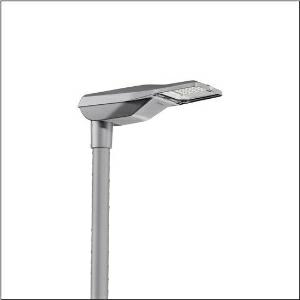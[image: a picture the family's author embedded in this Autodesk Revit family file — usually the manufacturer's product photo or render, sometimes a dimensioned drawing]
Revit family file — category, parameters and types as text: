
# Revit family: streetlight_sl_21_iq_micro___stw1_0a_5xe1e41g08cb_8385
name_source: partatom
category: Lighting Fixtures
units: mm (PartAtom-declared; Revit-internal decimal feet)

## family parameters
Cut with Voids When Loaded = No
Host = Face
Light Source = No
Part Type = Normal
Room Calculation Point = No
Round Connector Dimension = Use Diameter
Shared = No

## types (1)
- --- (1 x LED, 2980 lm, 19.4 W, 4000K)
    Apparent Load = 19 VA
    CIE Flux Codes = 38 75 98 100 100
    Color Rendering = 70
    Color Temperature = 4000K
    Default Elevation = 1800 mm
    Description = Streetlight SL 21 iQ micro, mast luminaire, primary light control with lens, of PMMA, primary optical cover: cover, of toughened safety glass, transparent, light distribution: STW1.0a, light emission: direct distribution, primary light characteristic: asymmetric, installation type: post-top, side-entry, LED, High Power LED, rated luminous flux: 2.980lm, luminous efficacy: 154lm/W, light colour: 740, colour temperature: 4000K, control gear: iQ Street-Remote, control: Street-Remote, Auto-Match, Temp-Guard, Lumen-Switch, Night-Set, Smart-Wire, Light-Fading, Desk-Remote (wireless, voltage-free reading and setting of iQ features in the workshop via application-optimized NFC function/RFID function), optimised constant luminous flux control (CLO 2.0), pre-setting: linear dimming characteristic, mains connection: 220..240V, AC, 50/60Hz, start of lifetime: 19W, end of service life: 20W, reduction: 10W, luminaire housing, of diecast aluminium, powder-coated, SITECO metallic grey (DB 702S), corrosivity category C5 high according to DIN EN ISO 12944, please order mast flange separately, inclination adjustable: 0°, 5°, 10°, 15°, sealing non-destructively replaceable, multi-level sealing system, length: 528mm, width: 235mm, height: 110mm, mast flange for spigot size: 42mm (side-entry): 5XC10008XM4, 60/48mm (side-entry/post-top): 5XC10108XM2, 76/60mm (side-entry/post-top): 5XC10108XM1, protection rating (complete): IP66, insulation class (complete): insulation class II (safety insulation), certification: CE, ENEC, ENEC+, VDE, impact resistance: IK10, permissible operating ambient temperature for outdoor applications: -40..+50°C, standard-compliant lighting for roads and squares, packaging unit: 1 piece

Light Distribution: STW1.0a
    Height = 110 mm
    Lamp = 1 x LED
    Lamp Light Flux = 2980 lm
    Lamp Power = 19.4 W
    Lamp count = 1
    Length = 528 mm
    Luminous efficacy = 154 lm/W
    Manufacturer = Siteco
    ModVariant = No
    Model = 5XE1E41G08CB
    Number of Poles = 1
    OnlyDefault = Yes
    Power Factor = 1
    Product Name = Streetlight SL 21 iQ micro | STW1.0a
    Product group = mast luminaire | pylon top
    ProductGroupID = 6100
    Protection Class = Protection class II
    Protection Degree = IP 66
    RLX_Detail_Level = 1
    RLX_Emergency_Light_Flux = 0 lm
    RLX_Emergency_Type = 0
    RLX_Emergency_Type_DB = No
    RlxData = <blob elided: 98617 chars, md5=caf6e045>
    Socket = socket
    Standby Power = 0 W
    System Light Flux = 2980 lm
    System Power = 19 W
    Type Comments = factory setting: luminous flux: 100 % | dim-lin: 254 | 387 mA
    Type Image = l_1006881.jpg
    URL = http://relux.com
    VarID = @adj_138283
    Voltage = 0 V
    Weight = 0.00 kg
    Width = 235 mm

## geometry (parser evidence)
native form markers: Blend x4, Sweep x11
no freeform markers — native parametric forms only
